# Revit family: Midea_VRF_Indoor_4-way Cassette_MI-90(100,112,140)Q4_DHN1-D (2nd DC)-360°
name_source: partatom
category: Equipamento mecânico
units: mm (PartAtom-declared; Revit-internal decimal feet)

## family parameters
Com base no plano de trabalho = Não
Compartilhado = Não
Corte com vazios quando carregada = Não
Cota do conector redondo = Utilizar diâmetro
Número OmniClass = 23.75.00.00
Ponto de cálculo do ambiente = Não
Sempre na vertical = Sim
Tipo de parte = Normal
Título OmniClass = Climate Control (HVAC)

## types (4) — shared parameters
Condensation = air
Depth = 840  [stored 2.75591 ft]
Descrição = High efficiency air cooled
Drain pipe = 32  [stored 0.104987 ft]
Fabricante = Trane
Gas = R410a
Gas pipe = 15.9  [stored 0.0521654 ft]
Height = 300
Installation = Indoor installation
Liquid pipe = 9.53
Machine material = grilles：ABS/HIPS
Maximum Fuse Amps = 15 A
Minimum Circuit Amps = 1 A
Panel color = S1004
Power supply = 220-240V ~50/60Hz
Series = Ultra
URL = https://www.trane.com
Width = 840  [stored 2.75591 ft]
clearance access behind = 1000  [stored 3.28084 ft]
clearance access front = 1000  [stored 3.28084 ft]
clearance access left = 1000  [stored 3.28084 ft]
clearance access right = 1000  [stored 3.28084 ft]

## per-type parameters (varying)
| type | Air Flow | Cooling Capacity | Cooling Power Input | Gross Weight | Heating Capacity | Heating Power Input |
| 4TVC0030EF000AA | 1264/1195/1117/1055/975/893/811 m3/h | 9.00 kW | 75 W | 28.40 kg | 10.00 kW | 75 W |
| 4TVC0034EF000AA | 1596/1477/1365/1239/1154/1087/1034 m3/h | 10.00 kW | 75 W | 28.40 kg | 11.00 kW | 75 W |
| 4TVC0038EF000AA | 1596/1477/1365/1239/1154/1087/1034 m3/h | 11.20 kW | 75 W | 28.40 kg | 12.50 kW | 75 W |
| 4TVC0048EF000AA | 1700/1600/1440/1250/1200/1150 m3/h | 14.00 kW | 94 W | 30.70 kg | 16.00 kW | 94 W |

note: column(s) folded — value = type name in every type: Modelo

note: [stored X ft] marks values corroborated as IEEE doubles in the binary element streams (Revit-internal decimal feet)

## geometry (parser evidence)
native form markers: Blend x2, Sweep x6
no freeform markers — native parametric forms only
